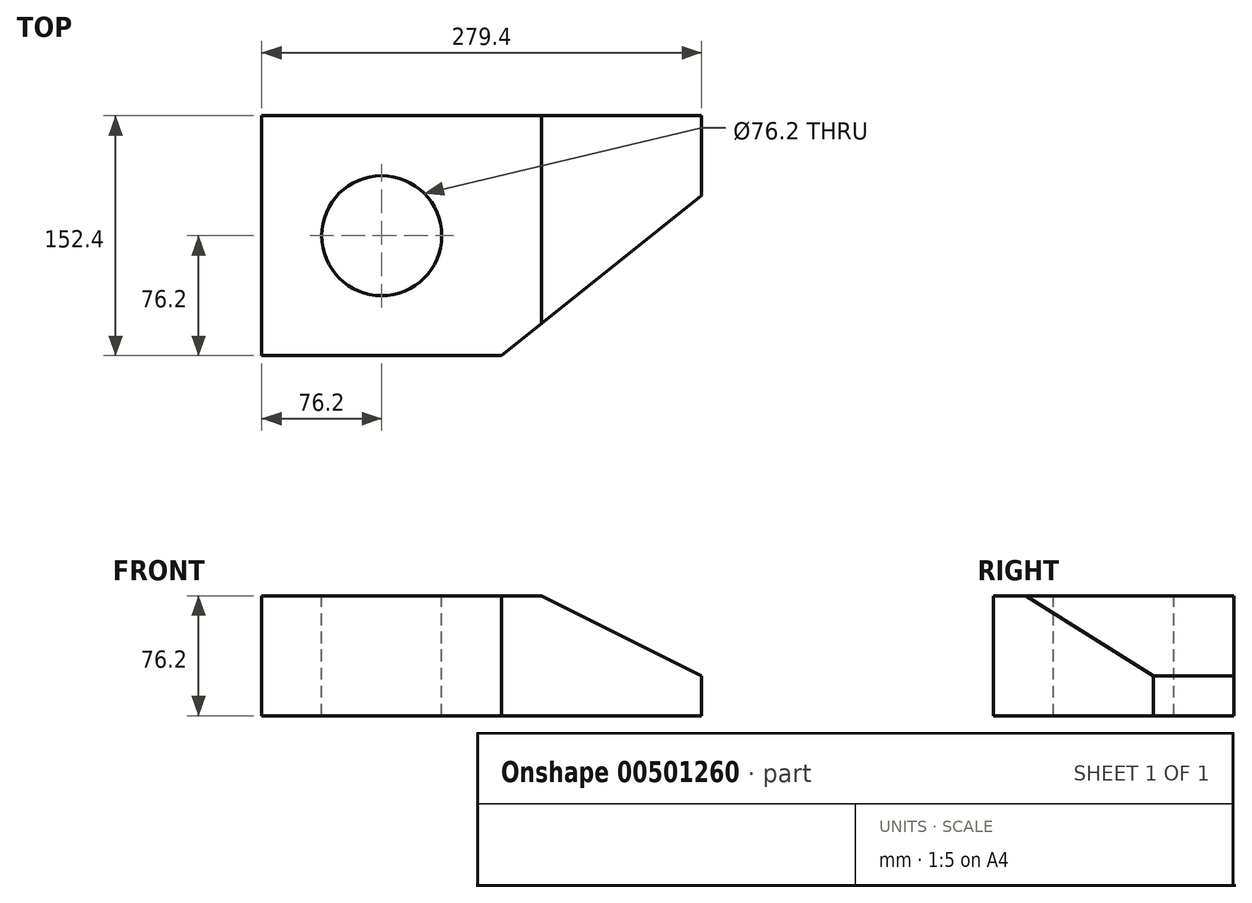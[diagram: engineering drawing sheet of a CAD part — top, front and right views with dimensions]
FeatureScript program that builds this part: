
annotation { "Feature Type Name" : "Feature", "Feature Type Description" : "" }
export const myFeature = defineFeature(function(context is Context, id is Id, definition is map)
    precondition{}
    {
        {
            var Q0;
            Q0=qCreatedBy(makeId("Front.planeOp"),FACE);
            var sketch = newSketch(context, id + "F0", { "sketchPlane" : qUnion([Q0])});
            skLineSegment(sketch, "E0.bottom", {"start": v(139.7, 38.1) * mm, "end": v(-139.7, 38.1) * mm});
            skLineSegment(sketch, "E0.top", {"start": v(139.7, -38.1) * mm, "end": v(-139.7, -38.1) * mm});
            skLineSegment(sketch, "E0.left", {"start": v(139.7, 38.1) * mm, "end": v(139.7, -38.1) * mm});
            skLineSegment(sketch, "E0.right", {"start": v(-139.7, 38.1) * mm, "end": v(-139.7, -38.1) * mm});
            skPoint(sketch, "E0.middle", {"position": v(0, 0) * mm});
            skSolve(sketch);
        }
        {
            var Q0;
            Q0 = qSketchRegion(id + "F0", true);
            extrude(context, id + "F1", {"entities" : qUnion([Q0]), "depth" : 152.4 * mm});
        }
        {
            var Q0;
            Q0=makeQuery(id+"F1.opExtrude","SWEPT_FACE",FACE,{"disambiguationData":[OSD([sQuery(id+"F0.wireOp",EDGE,"E0.bottom")])]});
            var sketch = newSketch(context, id + "F2", { "sketchPlane" : qUnion([Q0])});
            skLineSegment(sketch, "E1", {"start": v(139.7, -50.8) * mm, "end": v(12.7, -152.4) * mm});
            skLineSegment(sketch, "E2", {"start": v(12.7, -152.4) * mm, "end": v(139.7, -152.4) * mm});
            skLineSegment(sketch, "E3", {"start": v(139.7, -152.4) * mm, "end": v(139.7, -50.8) * mm});
            skSolve(sketch);
        }
        {
            var Q0;
            Q0 = qSketchRegion(id + "F2", true);
            extrude(context, id + "F3", {"entities" : qUnion([Q0]), "operationType" : NewBodyOperationType.REMOVE, "oppositeDirection" : true, "depth" : 125.1 * mm});
        }
        {
            var Q0;
            Q0=makeQuery(id+"F1.opExtrude","SWEPT_EDGE",EDGE,{"disambiguationData":[OSD([sQuery(id+"F0.wireOp",EDGE,"E0.bottom"),sQuery(id+"F0.wireOp",EDGE,"E0.left")])]});
            chamfer(context, id + "F4", {"entities" : qUnion([Q0]), "chamferType" : ChamferType.TWO_OFFSETS, "width1" : 101.6 * mm, "oppositeDirection" : false, "width2" : 50.8 * mm, "tangentPropagation" : true});
        }
        {
            var Q0;
            Q0=makeQuery(id+"F1.opExtrude","SWEPT_FACE",FACE,{"disambiguationData":[OSD([sQuery(id+"F0.wireOp",EDGE,"E0.bottom")])]});
            var sketch = newSketch(context, id + "F5", { "sketchPlane" : qUnion([Q0])});
            skCircle(sketch, "E4", {"center": v(-63.5, -76.2) * mm, "radius": 38.1 * mm});
            skSolve(sketch);
        }
        {
            var Q0;
            Q0 = qSketchRegion(id + "F5", true);
            extrude(context, id + "F6", {"entities" : qUnion([Q0]), "operationType" : NewBodyOperationType.REMOVE, "oppositeDirection" : true, "depth" : 200.53 * mm});
        }
    });
